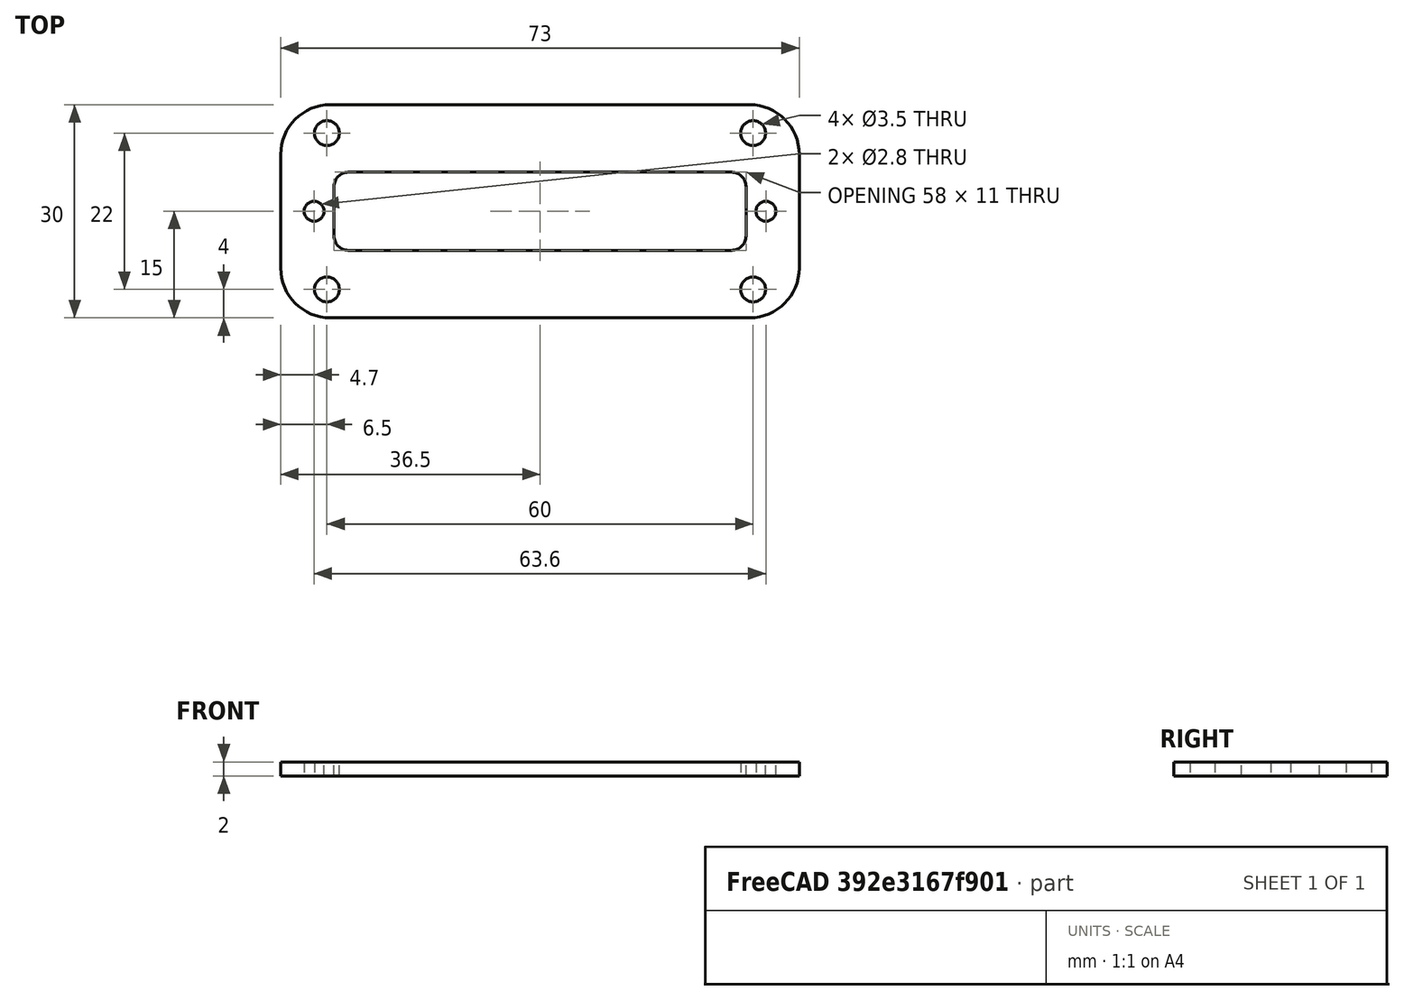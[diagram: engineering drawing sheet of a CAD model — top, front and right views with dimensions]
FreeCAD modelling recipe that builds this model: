
FCSTD DOCUMENT  (FreeCAD 0.19R)
Label: DBAdapter
License: All rights reserved
LicenseURL: http://en.wikipedia.org/wiki/All_rights_reserved
objects: PartDesign::Fillet×2, Mesh::Feature×2, Sketcher::SketchObject×1, PartDesign::Pad×1, PartDesign::Body×1
note: 8 computed .brp shape members not serialized (recipe doc carries the construction recipe); baked Part::Feature solids carry a one-line shape summary decoded from their .brp

FEATURE [Sketcher::SketchObject] Sketch
  FullyConstrained = true
  MapMode = 5
  Support = -> [XY_Plane]
  sketch-geometry (14):
    g0: Circle CenterX=-30 CenterY=11 CenterZ=0 NormalX=0 NormalY=0 NormalZ=1 AngleXU=0 Radius=1.75
    g1: Circle CenterX=30 CenterY=11 CenterZ=0 NormalX=0 NormalY=0 NormalZ=1 AngleXU=0 Radius=1.75
    g2: Circle CenterX=-30 CenterY=-11 CenterZ=0 NormalX=0 NormalY=0 NormalZ=1 AngleXU=0 Radius=1.75
    g3: Circle CenterX=30 CenterY=-11 CenterZ=0 NormalX=0 NormalY=0 NormalZ=1 AngleXU=0 Radius=1.75
    g4: LineSegment StartX=-36.5 StartY=15 StartZ=0 EndX=36.5 EndY=15 EndZ=0
    g5: LineSegment StartX=36.5 StartY=15 StartZ=0 EndX=36.5 EndY=-15 EndZ=0
    g6: LineSegment StartX=36.5 StartY=-15 StartZ=0 EndX=-36.5 EndY=-15 EndZ=0
    g7: LineSegment StartX=-36.5 StartY=-15 StartZ=0 EndX=-36.5 EndY=15 EndZ=0
    g8: LineSegment StartX=-29 StartY=5.5 StartZ=0 EndX=29 EndY=5.5 EndZ=0
    g9: LineSegment StartX=29 StartY=5.5 StartZ=0 EndX=29 EndY=-5.5 EndZ=0
    g10: LineSegment StartX=29 StartY=-5.5 StartZ=0 EndX=-29 EndY=-5.5 EndZ=0
    g11: LineSegment StartX=-29 StartY=-5.5 StartZ=0 EndX=-29 EndY=5.5 EndZ=0
    g12: Circle CenterX=-31.8 CenterY=0 CenterZ=0 NormalX=0 NormalY=0 NormalZ=1 AngleXU=0 Radius=1.4
    g13: Circle CenterX=31.8 CenterY=0 CenterZ=0 NormalX=0 NormalY=0 NormalZ=1 AngleXU=0 Radius=1.4
  constraints (35):
    c: Symmetric(g3,g2,g-2)
    c: Symmetric(g3,g1,g-1)
    c: Symmetric(g1,g0,g-2)
    c: Distance(g0,g1) = 60
    c: Distance(g3,g1) = 22
    c: Diameter(g0) = 3.5
    c: Equal(g0,g1)
    c: Equal(g0,g2)
    c: Equal(g0,g3)
    c: Coincident(g4,g5)
    c: Coincident(g5,g6)
    c: Coincident(g6,g7)
    c: Coincident(g7,g4)
    c: Horizontal(g4)
    c: Horizontal(g6)
    c: Vertical(g5)
    c: Vertical(g7)
    c: Symmetric(g4,g6,g-1)
    c: Distance(g7) = 30
    c: Distance(g4) = 73
    c: Coincident(g8,g9)
    c: Coincident(g9,g10)
    c: Coincident(g10,g11)
    c: Coincident(g11,g8)
    c: Horizontal(g10)
    c: Vertical(g9)
    c: Symmetric(g10,g8,g-1)
    c: Symmetric(g8,g10,g-1)
    c: Distance(g11) = 11
    c: Distance(g8) = 58
    c: PointOnObject(g13,g-1)
    c: Diameter(g12) = 2.8
    c: Equal(g12,g13)
    c: Symmetric(g12,g13,g-1)
    c: Distance(g13,g12) = 63.6
FEATURE [PartDesign::Pad] Pad
  Direction = (1,1,1)
  Length = 2
  Length2 = 100
  Profile = -> Sketch
  Type = 0
FEATURE [PartDesign::Fillet] Fillet
  Base = -> Pad [Edge14,Edge20,Edge13,Edge17]
  BaseFeature = -> Pad
  Radius = 2
  SupportTransform = false
FEATURE [Mesh::Feature] Mesh  label="Fillet001 (Meshed)"
FEATURE [PartDesign::Fillet] Fillet001
  Base = -> Fillet [Edge47,Edge46,Edge45,Edge48]
  BaseFeature = -> Fillet
  Radius = 7
  SupportTransform = false
FEATURE [PartDesign::Body] Body
  Group = -> [Sketch,Pad,Fillet,Fillet001]
  Origin = -> Origin
  Tip = -> Fillet001
FEATURE [Mesh::Feature] Mesh001  label="Fillet001 (Meshed)001"
